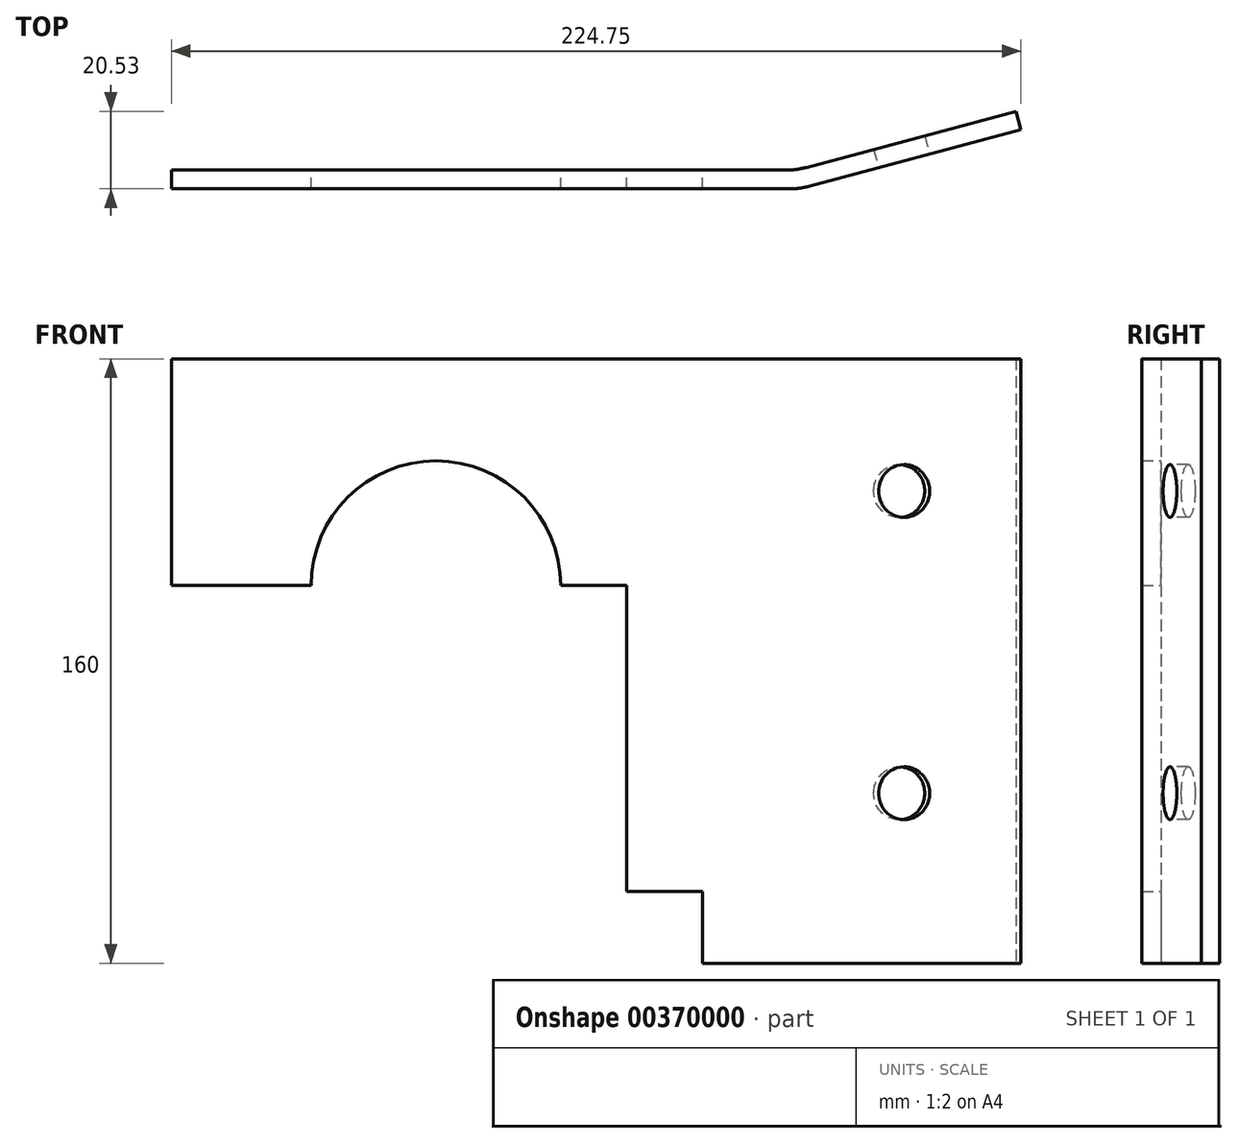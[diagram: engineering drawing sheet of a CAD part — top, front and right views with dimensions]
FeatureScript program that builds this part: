
annotation { "Feature Type Name" : "Feature", "Feature Type Description" : "" }
export const myFeature = defineFeature(function(context is Context, id is Id, definition is map)
    precondition{}
    {
        {
            var Q0;
            Q0=qCreatedBy(makeId("Top.planeOp"),FACE);
            var sketch = newSketch(context, id + "F0", { "sketchPlane" : qUnion([Q0])});
            skLineSegment(sketch, "E0", {"start": v(-70, -5) * mm, "end": v(-70, 0) * mm});
            skLineSegment(sketch, "E1", {"start": v(-70, 0) * mm, "end": v(92.87, 0) * mm});
            skLineSegment(sketch, "E2", {"start": v(98.04, 0.68) * mm, "end": v(153.46, 15.53) * mm});
            skLineSegment(sketch, "E3", {"start": v(154.75, 10.7) * mm, "end": v(98.7, -4.32) * mm});
            skLineSegment(sketch, "E4", {"start": v(93.53, -5) * mm, "end": v(-70, -5) * mm});
            skLineSegment(sketch, "E5", {"start": v(154.75, 10.7) * mm, "end": v(153.46, 15.53) * mm});
            skPoint(sketch, "E6.visualSharp", {"position": v(95.5, 0) * mm});
            skArc(sketch, "E6.filletArc", {"start": v(92.87, 0) * mm, "mid": v(95.48, 0.17) * mm, "end": v(98.04, 0.68) * mm});
            skPoint(sketch, "E7.visualSharp", {"position": v(96.16, -5) * mm});
            skArc(sketch, "E7.filletArc", {"start": v(93.53, -5) * mm, "mid": v(96.14, -4.83) * mm, "end": v(98.7, -4.32) * mm});
            skSolve(sketch);
        }
        {
            var Q0;
            Q0 = qSketchRegion(id + "F0", true);
            extrude(context, id + "F1", {"entities" : qUnion([Q0]), "depth" : 60 * mm, "hasSecondDirection" : true, "secondDirectionOppositeDirection" : true, "secondDirectionDepth" : 100 * mm});
        }
        {
            var Q0;
            Q0=qCreatedBy(makeId("Front.planeOp"),FACE);
            var sketch = newSketch(context, id + "F2", { "sketchPlane" : qUnion([Q0])});
            skArc(sketch, "E8", {"start": v(33, 0) * mm, "mid": v(0, 33) * mm, "end": v(-33, 0) * mm});
            skLineSegment(sketch, "E9", {"start": v(-33, 0) * mm, "end": v(-70, 0) * mm});
            skLineSegment(sketch, "E10", {"start": v(-70, 0) * mm, "end": v(-70, 60) * mm, "construction": true});
            skLineSegment(sketch, "E11", {"start": v(-70, 60) * mm, "end": v(95.5, 60) * mm, "construction": true});
            skCircle(sketch, "E12", {"center": v(128.4, 40) * mm, "radius": 10.44 * mm, "construction": true});
            skCircle(sketch, "E13", {"center": v(128.4, -40) * mm, "radius": 9.98 * mm, "construction": true});
            skLineSegment(sketch, "E14", {"start": v(128.4, 40) * mm, "end": v(128.4, -40) * mm, "construction": true});
            skPoint(sketch, "E15", {"position": v(128.4, 0) * mm});
            skLineSegment(sketch, "E16", {"start": v(33, 0) * mm, "end": v(50.5, 0) * mm});
            skLineSegment(sketch, "E17", {"start": v(50.5, 0) * mm, "end": v(50.5, -81) * mm});
            skLineSegment(sketch, "E18", {"start": v(50.5, -81) * mm, "end": v(70.5, -81) * mm});
            skLineSegment(sketch, "E19", {"start": v(70.5, -81) * mm, "end": v(70.5, -101) * mm});
            skLineSegment(sketch, "E20", {"start": v(70.5, -101) * mm, "end": v(95.5, -101) * mm, "construction": true});
            skLineSegment(sketch, "E21", {"start": v(95.5, -101) * mm, "end": v(95.5, 60) * mm, "construction": true});
            skLineSegment(sketch, "E22", {"start": v(70.5, -101) * mm, "end": v(-70, -101) * mm});
            skLineSegment(sketch, "E23", {"start": v(-70, -101) * mm, "end": v(-70, 0) * mm});
            skSolve(sketch);
        }
        {
            var Q0;
            Q0 = qSketchRegion(id + "F2", true);
            extrude(context, id + "F3", {"entities" : qUnion([Q0]), "operationType" : NewBodyOperationType.REMOVE, "depth" : 25 * mm});
        }
        {
            var Q0;
            Q0=makeQuery(id+"F1.opExtrude","SWEPT_FACE",FACE,{"disambiguationData":[OSD([sQuery(id+"F0.wireOp",EDGE,"E3")])]});
            var sketch = newSketch(context, id + "F4", { "sketchPlane" : qUnion([Q0])});
            skCircle(sketch, "E24", {"center": v(120.25, 25) * mm, "radius": 7 * mm});
            skCircle(sketch, "E25", {"center": v(120.25, -55) * mm, "radius": 7 * mm});
            skSolve(sketch);
        }
        {
            var Q0;
            Q0 = qSketchRegion(id + "F4", true);
            extrude(context, id + "F5", {"entities" : qUnion([Q0]), "operationType" : NewBodyOperationType.REMOVE, "oppositeDirection" : true, "depth" : 25 * mm});
        }
    });
